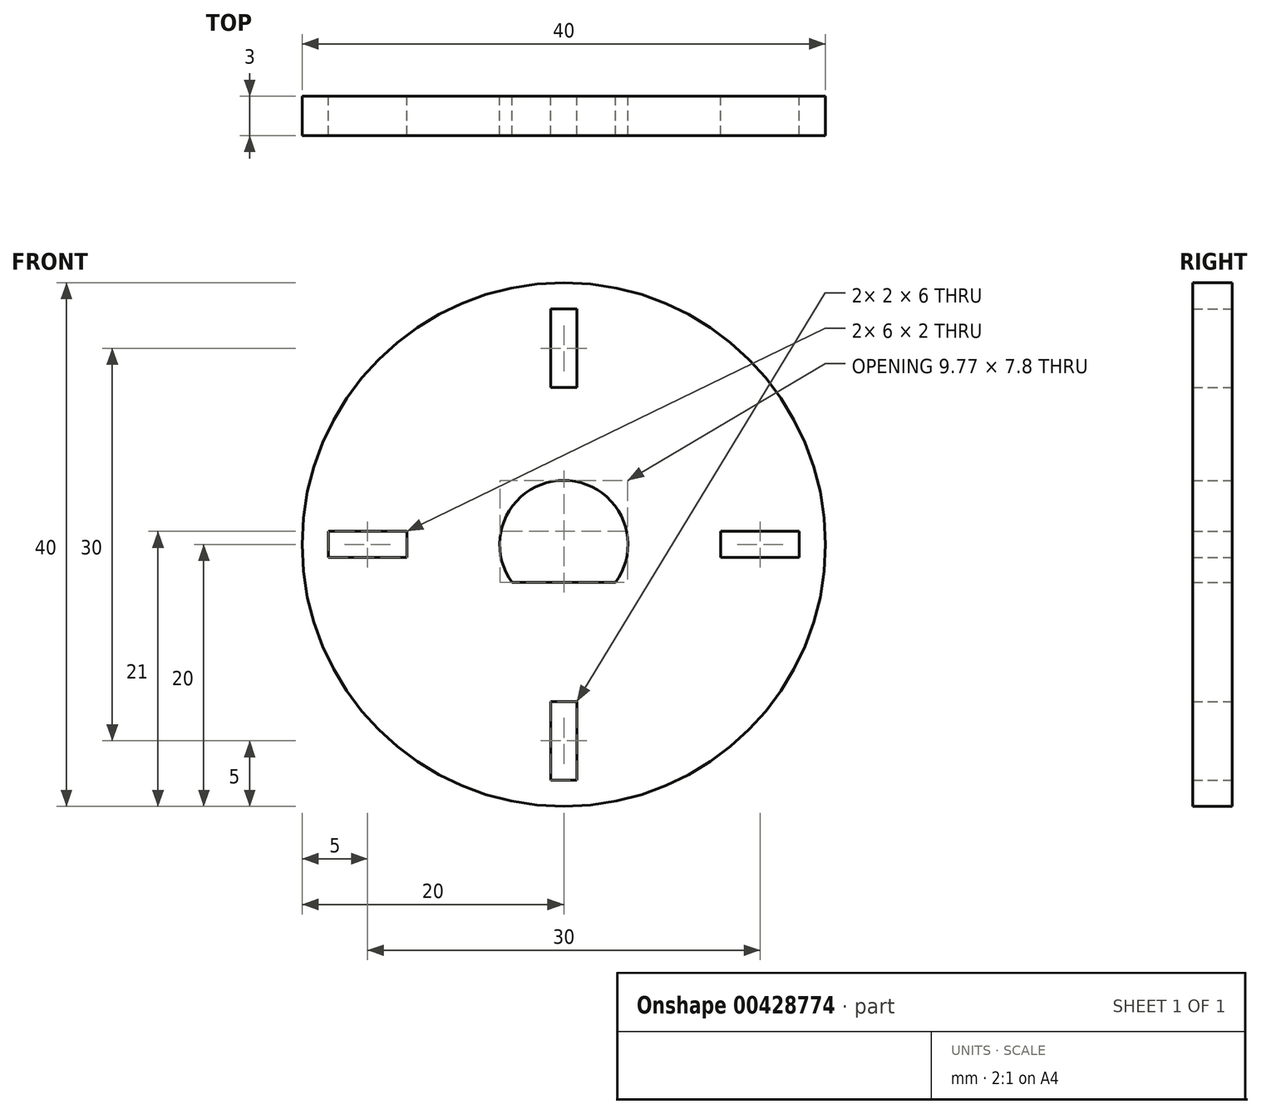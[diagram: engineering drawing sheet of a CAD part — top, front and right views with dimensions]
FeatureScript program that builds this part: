
annotation { "Feature Type Name" : "Feature", "Feature Type Description" : "" }
export const myFeature = defineFeature(function(context is Context, id is Id, definition is map)
    precondition{}
    {
        {
            var Q0;
            Q0=qCreatedBy(makeId("Front.planeOp"),FACE);
            var sketch = newSketch(context, id + "F0", { "sketchPlane" : qUnion([Q0])});
            skCircle(sketch, "E0", {"center": v(0, 0) * mm, "radius": 20 * mm});
            skArc(sketch, "E1", {"start": v(3.95, -2.9) * mm, "mid": v(0, 4.9) * mm, "end": v(-3.95, -2.9) * mm});
            skLineSegment(sketch, "E2", {"start": v(0, 4.9) * mm, "end": v(0, -2.9) * mm, "construction": true});
            skLineSegment(sketch, "E3", {"start": v(-3.95, -2.9) * mm, "end": v(3.95, -2.9) * mm});
            skLineSegment(sketch, "E4", {"start": v(0, 12) * mm, "end": v(1, 12) * mm});
            skLineSegment(sketch, "E5", {"start": v(1, 12) * mm, "end": v(1, 18) * mm});
            skLineSegment(sketch, "E6", {"start": v(1, 18) * mm, "end": v(-1, 18) * mm});
            skLineSegment(sketch, "E7", {"start": v(0, 12) * mm, "end": v(-1, 12) * mm});
            skLineSegment(sketch, "E8", {"start": v(-1, 12) * mm, "end": v(-1, 18) * mm});
            skLineSegment(sketch, "E9.1.0", {"start": v(-12, 0) * mm, "end": v(-12, 1) * mm});
            skLineSegment(sketch, "E9.1.1", {"start": v(-12, 1) * mm, "end": v(-18, 1) * mm});
            skLineSegment(sketch, "E9.1.2", {"start": v(-12, -1) * mm, "end": v(-18, -1) * mm});
            skLineSegment(sketch, "E9.1.3", {"start": v(-12, 0) * mm, "end": v(-12, -1) * mm});
            skLineSegment(sketch, "E9.1.4", {"start": v(-18, 1) * mm, "end": v(-18, -1) * mm});
            skLineSegment(sketch, "E9.2.0", {"start": v(0, -12) * mm, "end": v(-1, -12) * mm});
            skLineSegment(sketch, "E9.2.1", {"start": v(-1, -12) * mm, "end": v(-1, -18) * mm});
            skLineSegment(sketch, "E9.2.2", {"start": v(1, -12) * mm, "end": v(1, -18) * mm});
            skLineSegment(sketch, "E9.2.3", {"start": v(0, -12) * mm, "end": v(1, -12) * mm});
            skLineSegment(sketch, "E9.2.4", {"start": v(-1, -18) * mm, "end": v(1, -18) * mm});
            skLineSegment(sketch, "E9.3.0", {"start": v(12, 0) * mm, "end": v(12, -1) * mm});
            skLineSegment(sketch, "E9.3.1", {"start": v(12, -1) * mm, "end": v(18, -1) * mm});
            skLineSegment(sketch, "E9.3.2", {"start": v(12, 1) * mm, "end": v(18, 1) * mm});
            skLineSegment(sketch, "E9.3.3", {"start": v(12, 0) * mm, "end": v(12, 1) * mm});
            skLineSegment(sketch, "E9.3.4", {"start": v(18, -1) * mm, "end": v(18, 1) * mm});
            skSolve(sketch);
        }
        {
            var Q0;
            Q0=makeQuery(id+"F0.imprint","IMPRINT",FACE,{"disambiguationData":[TD([[makeQuery(id+"F0.imprint","IMPRINT",EDGE,{"derivedFrom":sQuery(id+"F0.wireOp",EDGE,"E0")}),1.0]])]});
            extrude(context, id + "F1", {"entities" : qUnion([Q0]), "depth" : 3 * mm});
        }
    });
